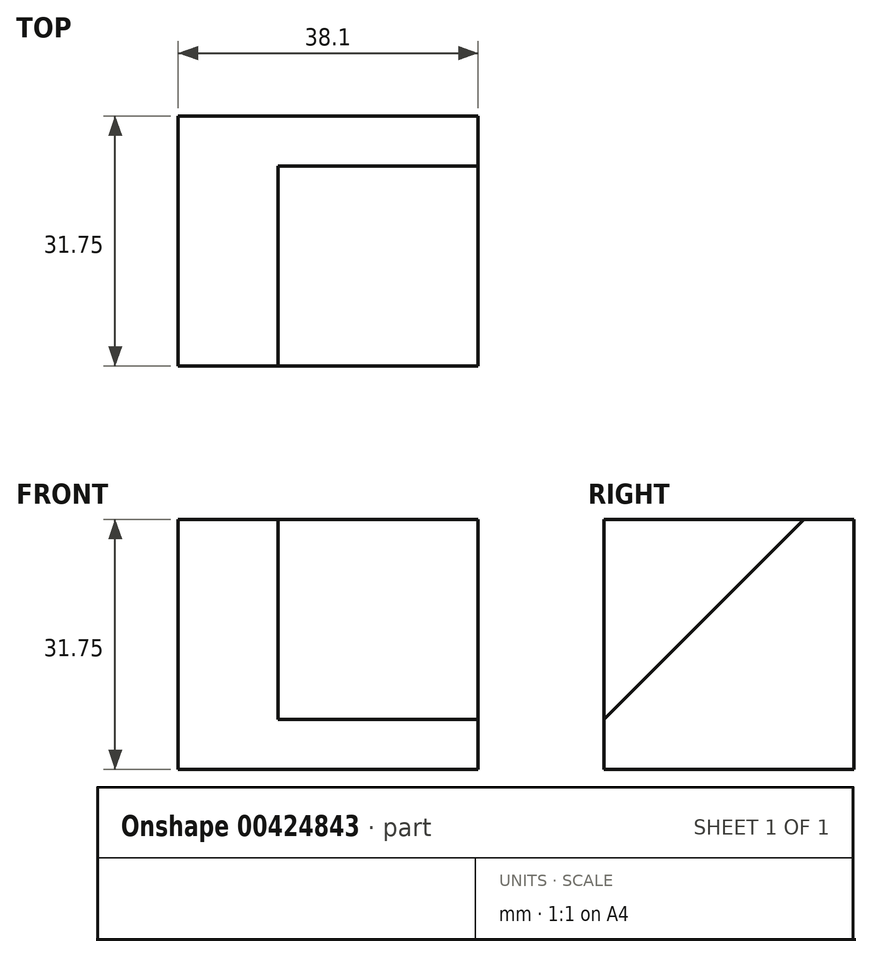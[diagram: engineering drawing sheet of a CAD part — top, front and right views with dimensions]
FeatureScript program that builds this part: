
annotation { "Feature Type Name" : "Feature", "Feature Type Description" : "" }
export const myFeature = defineFeature(function(context is Context, id is Id, definition is map)
    precondition{}
    {
        {
            var Q0;
            Q0=qCreatedBy(makeId("Front.planeOp"),FACE);
            var sketch = newSketch(context, id + "F0", { "sketchPlane" : qUnion([Q0])});
            skLineSegment(sketch, "E0", {"start": v(0, 0) * mm, "end": v(38.1, 0) * mm});
            skLineSegment(sketch, "E1", {"start": v(38.1, 0) * mm, "end": v(38.1, 6.35) * mm});
            skLineSegment(sketch, "E2", {"start": v(38.1, 6.35) * mm, "end": v(12.7, 6.35) * mm});
            skLineSegment(sketch, "E3", {"start": v(12.7, 6.35) * mm, "end": v(12.7, 31.75) * mm});
            skLineSegment(sketch, "E4", {"start": v(12.7, 31.75) * mm, "end": v(0, 31.75) * mm});
            skLineSegment(sketch, "E5", {"start": v(0, 31.75) * mm, "end": v(0, 0) * mm});
            skSolve(sketch);
        }
        {
            var Q0;
            Q0=makeQuery(id+"F0.imprint","IMPRINT",FACE,{"disambiguationData":[TD([[makeQuery(id+"F0.imprint","IMPRINT",EDGE,{"derivedFrom":sQuery(id+"F0.wireOp",EDGE,"E0")}),1.0]])]});
            extrude(context, id + "F1", {"entities" : qUnion([Q0]), "depth" : 25.4 * mm});
        }
        {
            var Q0;
            Q0=qCreatedBy(makeId("Top.planeOp"),FACE);
            var sketch = newSketch(context, id + "F2", { "sketchPlane" : qUnion([Q0])});
            skLineSegment(sketch, "E6", {"start": v(0, 0) * mm, "end": v(0, 6.35) * mm});
            skLineSegment(sketch, "E7", {"start": v(0, 6.35) * mm, "end": v(38.1, 6.35) * mm});
            skLineSegment(sketch, "E8", {"start": v(38.1, 6.35) * mm, "end": v(38.1, 0) * mm});
            skLineSegment(sketch, "E9", {"start": v(38.1, 0) * mm, "end": v(12.7, 0) * mm});
            skLineSegment(sketch, "E10", {"start": v(12.7, 0) * mm, "end": v(12.7, -25.9) * mm});
            skLineSegment(sketch, "E11", {"start": v(38.1, 0) * mm, "end": v(38.1, -25.9) * mm});
            skLineSegment(sketch, "E12", {"start": v(0, 0) * mm, "end": v(0, -25.4) * mm});
            skLineSegment(sketch, "E13", {"start": v(0, -25.4) * mm, "end": v(12.7, -25.4) * mm});
            skSolve(sketch);
        }
        {
            var Q0;
            Q0=makeQuery(id+"F2.imprint","IMPRINT",FACE,{"disambiguationData":[TD([[makeQuery(id+"F2.imprint","IMPRINT",EDGE,{"derivedFrom":sQuery(id+"F2.wireOp",EDGE,"E6")}),-1.0]])]});
            extrude(context, id + "F3", {"entities" : qUnion([Q0]), "operationType" : NewBodyOperationType.ADD, "depth" : 31.75 * mm});
        }
        {
            var Q0;
            Q0=makeQuery(id+"F3.boolean.opBoolean","MERGE",FACE,{"derivedFrom":[makeQuery(id+"F1.opExtrude","SWEPT_FACE",FACE,{"disambiguationData":[OSD([sQuery(id+"F0.wireOp",EDGE,"E1")])]}),makeQuery(id+"F3.opExtrude","SWEPT_FACE",FACE,{"disambiguationData":[OSD([sQuery(id+"F2.wireOp",EDGE,"E8")])]})]});
            var sketch = newSketch(context, id + "F4", { "sketchPlane" : qUnion([Q0])});
            skLineSegment(sketch, "E14", {"start": v(0, 0) * mm, "end": v(6.35, 0) * mm});
            skLineSegment(sketch, "E15", {"start": v(6.35, 0) * mm, "end": v(6.35, 31.75) * mm});
            skLineSegment(sketch, "E16", {"start": v(6.35, 31.75) * mm, "end": v(0, 31.75) * mm});
            skLineSegment(sketch, "E17", {"start": v(0, 31.75) * mm, "end": v(-25.4, 6.35) * mm});
            skLineSegment(sketch, "E18", {"start": v(-25.4, 6.35) * mm, "end": v(-25.4, 0) * mm});
            skLineSegment(sketch, "E19", {"start": v(-25.4, 0) * mm, "end": v(0, 0) * mm});
            skSolve(sketch);
        }
        {
            var Q0;
            Q0=makeQuery(id+"F4.imprint","IMPRINT",FACE,{"disambiguationData":[TD([[makeQuery(id+"F4.imprint","IMPRINT",EDGE,{"derivedFrom":sQuery(id+"F4.wireOp",EDGE,"E17")}),1.0]])]});
            extrude(context, id + "F5", {"entities" : qUnion([Q0]), "operationType" : NewBodyOperationType.ADD, "oppositeDirection" : true, "depth" : 25.9 * mm});
        }
    });
